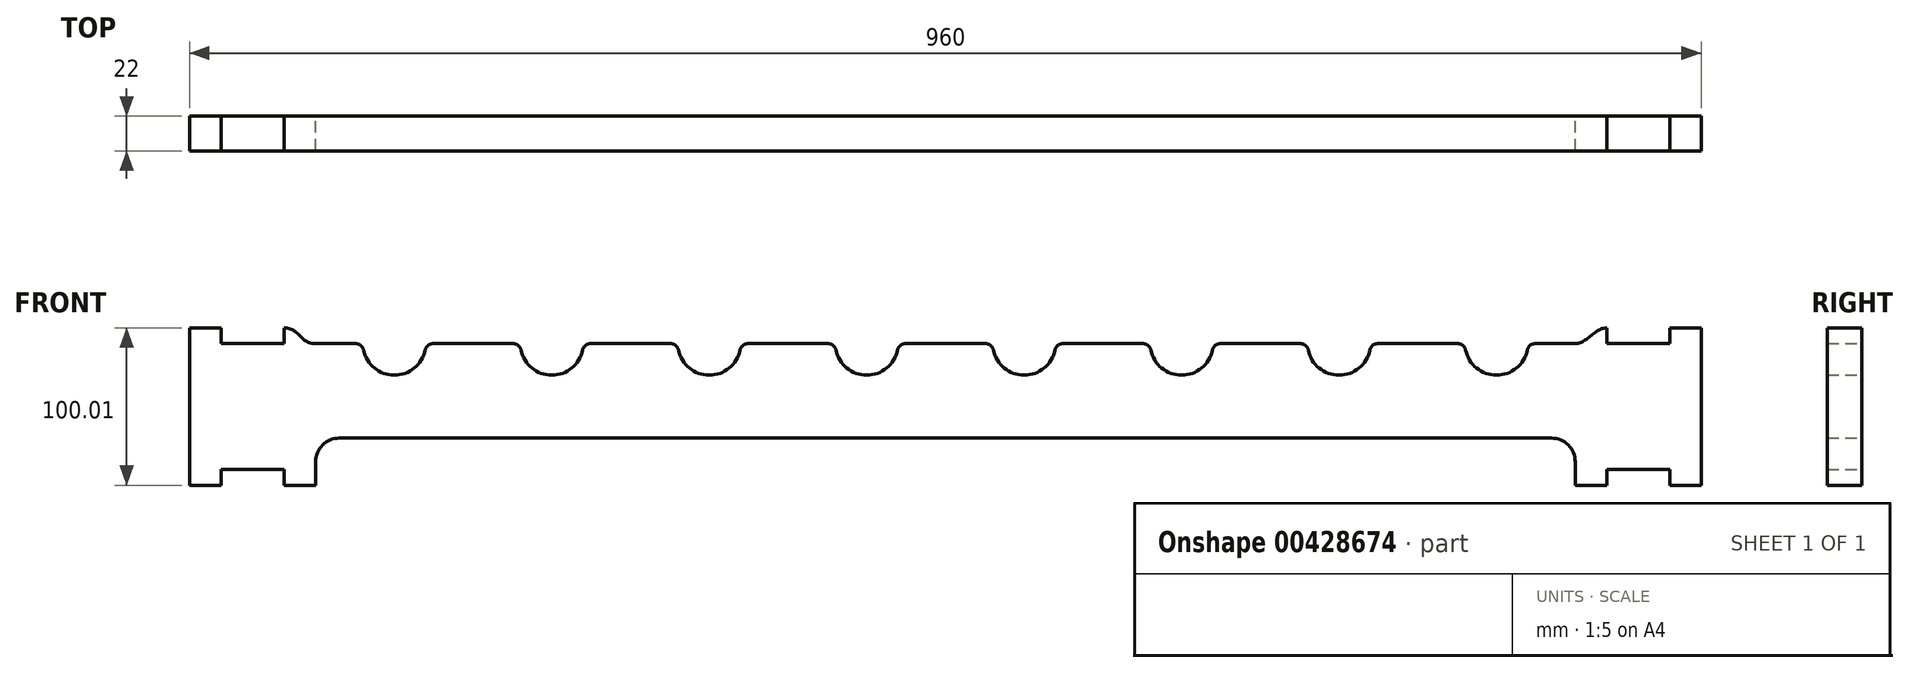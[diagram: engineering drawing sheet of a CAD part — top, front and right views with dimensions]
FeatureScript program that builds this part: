
annotation { "Feature Type Name" : "Feature", "Feature Type Description" : "" }
export const myFeature = defineFeature(function(context is Context, id is Id, definition is map)
    precondition{}
    {
        {
            var Q0;
            Q0=qCreatedBy(makeId("Front.planeOp"),FACE);
            var sketch = newSketch(context, id + "F0", { "sketchPlane" : qUnion([Q0])});
            skLineSegment(sketch, "E0.bottom", {"start": v(476.5, 50) * mm, "end": v(456.5, 50) * mm});
            skLineSegment(sketch, "E0.top", {"start": v(476.5, -50) * mm, "end": v(456.5, -50) * mm});
            skPoint(sketch, "E0.middle", {"position": v(0, 0) * mm});
            skArc(sketch, "E1", {"start": v(-373.1, 36) * mm, "mid": v(-353.5, 20) * mm, "end": v(-333.9, 36) * mm});
            skArc(sketch, "E2", {"start": v(-273.1, 36) * mm, "mid": v(-253.5, 20) * mm, "end": v(-233.9, 36) * mm});
            skArc(sketch, "E3", {"start": v(-173.1, 36) * mm, "mid": v(-153.5, 20) * mm, "end": v(-133.9, 36) * mm});
            skArc(sketch, "E4", {"start": v(-73.1, 36) * mm, "mid": v(-53.5, 20) * mm, "end": v(-33.9, 36) * mm});
            skArc(sketch, "E5", {"start": v(26.9, 36) * mm, "mid": v(46.5, 20) * mm, "end": v(66.1, 36) * mm});
            skArc(sketch, "E6", {"start": v(126.9, 36) * mm, "mid": v(146.5, 20) * mm, "end": v(166.1, 36) * mm});
            skArc(sketch, "E7", {"start": v(226.9, 36) * mm, "mid": v(246.5, 20) * mm, "end": v(266.1, 36) * mm});
            skArc(sketch, "E8", {"start": v(326.9, 36) * mm, "mid": v(346.5, 20) * mm, "end": v(366.1, 36) * mm});
            skLineSegment(sketch, "E9", {"start": v(456.5, 50) * mm, "end": v(476.5, 50) * mm});
            skLineSegment(sketch, "E10", {"start": v(476.5, 50) * mm, "end": v(476.5, -50) * mm});
            skLineSegment(sketch, "E11", {"start": v(416.5, -50) * mm, "end": v(416.5, -40) * mm});
            skLineSegment(sketch, "E12", {"start": v(416.5, -40) * mm, "end": v(456.5, -40) * mm});
            skLineSegment(sketch, "E13", {"start": v(456.5, 40) * mm, "end": v(416.5, 40) * mm});
            skLineSegment(sketch, "E14", {"start": v(416.5, 40) * mm, "end": v(416.5, 50) * mm});
            skLineSegment(sketch, "E15", {"start": v(456.5, 50) * mm, "end": v(456.5, 40) * mm});
            skLineSegment(sketch, "E16", {"start": v(456.5, -40) * mm, "end": v(456.5, -50) * mm});
            skLineSegment(sketch, "E17.trimOffspring", {"start": v(416.5, -50) * mm, "end": v(396.5, -50) * mm});
            skLineSegment(sketch, "E18", {"start": v(-422.71, 50) * mm, "end": v(-423.5, 50) * mm});
            skLineSegment(sketch, "E19", {"start": v(-463.5, 50) * mm, "end": v(-483.5, 50) * mm});
            skLineSegment(sketch, "E20", {"start": v(-483.5, 50) * mm, "end": v(-483.5, -50) * mm});
            skLineSegment(sketch, "E21", {"start": v(-483.5, -50) * mm, "end": v(-463.5, -50) * mm});
            skLineSegment(sketch, "E22", {"start": v(-423.5, -50) * mm, "end": v(-423.5, -40) * mm});
            skLineSegment(sketch, "E23", {"start": v(-423.5, -40) * mm, "end": v(-463.5, -40) * mm});
            skLineSegment(sketch, "E24", {"start": v(-463.5, 40) * mm, "end": v(-423.5, 40) * mm});
            skLineSegment(sketch, "E25", {"start": v(-423.5, 40) * mm, "end": v(-423.5, 50) * mm});
            skLineSegment(sketch, "E26", {"start": v(-463.5, 50) * mm, "end": v(-463.5, 40) * mm});
            skLineSegment(sketch, "E27", {"start": v(-463.5, -40) * mm, "end": v(-463.5, -50) * mm});
            skLineSegment(sketch, "E28.trimOffspring", {"start": v(-463.5, -50) * mm, "end": v(-483.5, -50) * mm});
            skLineSegment(sketch, "E29.trimOffspring", {"start": v(-329, 40) * mm, "end": v(-278, 40) * mm});
            skLineSegment(sketch, "E30.trimOffspring", {"start": v(-229, 40) * mm, "end": v(-178, 40) * mm});
            skLineSegment(sketch, "E31.trimOffspring", {"start": v(-129, 40) * mm, "end": v(-78, 40) * mm});
            skLineSegment(sketch, "E32.trimOffspring", {"start": v(-29, 40) * mm, "end": v(22, 40) * mm});
            skLineSegment(sketch, "E33.trimOffspring", {"start": v(71, 40) * mm, "end": v(122, 40) * mm});
            skLineSegment(sketch, "E34.trimOffspring", {"start": v(171, 40) * mm, "end": v(222, 40) * mm});
            skLineSegment(sketch, "E35.trimOffspring", {"start": v(271, 40) * mm, "end": v(322, 40) * mm});
            skLineSegment(sketch, "E36.trimOffspring", {"start": v(371, 40) * mm, "end": v(396.5, 40) * mm});
            skLineSegment(sketch, "E37", {"start": v(-403.5, 40) * mm, "end": v(-378, 40) * mm});
            skFitSpline(sketch, "E38", {"points": [v(-423.5, 50) * mm, v(-403.5, 40) * mm], "startDerivative": vector(28.84, 0.87) * mm, "endDerivative": vector(30, 0) * mm});
            skFitSpline(sketch, "E39", {"points": [v(396.5, 40) * mm, v(416.5, 50) * mm], "startDerivative": vector(21.98, 0) * mm, "endDerivative": vector(23.53, 0) * mm});
            skPoint(sketch, "E40.trimOffspring.start.orphan", {"position": v(-423.5, 40) * mm});
            skPoint(sketch, "E41.visualSharp", {"position": v(-373.5, 40) * mm});
            skArc(sketch, "E41.filletArc", {"start": v(-373.1, 36) * mm, "mid": v(-374.83, 38.87) * mm, "end": v(-378, 40) * mm});
            skPoint(sketch, "E42.visualSharp", {"position": v(-333.5, 40) * mm});
            skArc(sketch, "E42.filletArc", {"start": v(-329, 40) * mm, "mid": v(-332.17, 38.87) * mm, "end": v(-333.9, 36) * mm});
            skPoint(sketch, "E43.visualSharp", {"position": v(-273.5, 40) * mm});
            skArc(sketch, "E43.filletArc", {"start": v(-273.1, 36) * mm, "mid": v(-274.83, 38.87) * mm, "end": v(-278, 40) * mm});
            skPoint(sketch, "E44.visualSharp", {"position": v(-233.5, 40) * mm});
            skArc(sketch, "E44.filletArc", {"start": v(-229, 40) * mm, "mid": v(-232.17, 38.87) * mm, "end": v(-233.9, 36) * mm});
            skPoint(sketch, "E45.visualSharp", {"position": v(-173.5, 40) * mm});
            skArc(sketch, "E45.filletArc", {"start": v(-173.1, 36) * mm, "mid": v(-174.83, 38.87) * mm, "end": v(-178, 40) * mm});
            skPoint(sketch, "E46.visualSharp", {"position": v(-133.5, 40) * mm});
            skArc(sketch, "E46.filletArc", {"start": v(-129, 40) * mm, "mid": v(-132.17, 38.87) * mm, "end": v(-133.9, 36) * mm});
            skPoint(sketch, "E47.visualSharp", {"position": v(-73.5, 40) * mm});
            skArc(sketch, "E47.filletArc", {"start": v(-73.1, 36) * mm, "mid": v(-74.83, 38.87) * mm, "end": v(-78, 40) * mm});
            skPoint(sketch, "E48.visualSharp", {"position": v(-33.5, 40) * mm});
            skArc(sketch, "E48.filletArc", {"start": v(-29, 40) * mm, "mid": v(-32.17, 38.87) * mm, "end": v(-33.9, 36) * mm});
            skPoint(sketch, "E49.visualSharp", {"position": v(26.5, 40) * mm});
            skArc(sketch, "E49.filletArc", {"start": v(26.9, 36) * mm, "mid": v(25.17, 38.87) * mm, "end": v(22, 40) * mm});
            skPoint(sketch, "E50.visualSharp", {"position": v(66.5, 40) * mm});
            skArc(sketch, "E50.filletArc", {"start": v(71, 40) * mm, "mid": v(67.83, 38.87) * mm, "end": v(66.1, 36) * mm});
            skPoint(sketch, "E51.visualSharp", {"position": v(126.5, 40) * mm});
            skArc(sketch, "E51.filletArc", {"start": v(126.9, 36) * mm, "mid": v(125.17, 38.87) * mm, "end": v(122, 40) * mm});
            skPoint(sketch, "E52.visualSharp", {"position": v(166.5, 40) * mm});
            skArc(sketch, "E52.filletArc", {"start": v(171, 40) * mm, "mid": v(167.83, 38.87) * mm, "end": v(166.1, 36) * mm});
            skPoint(sketch, "E53.visualSharp", {"position": v(226.5, 40) * mm});
            skArc(sketch, "E53.filletArc", {"start": v(226.9, 36) * mm, "mid": v(225.17, 38.87) * mm, "end": v(222, 40) * mm});
            skPoint(sketch, "E54.visualSharp", {"position": v(266.5, 40) * mm});
            skArc(sketch, "E54.filletArc", {"start": v(271, 40) * mm, "mid": v(267.83, 38.87) * mm, "end": v(266.1, 36) * mm});
            skPoint(sketch, "E55.visualSharp", {"position": v(326.5, 40) * mm});
            skArc(sketch, "E55.filletArc", {"start": v(326.9, 36) * mm, "mid": v(325.17, 38.87) * mm, "end": v(322, 40) * mm});
            skPoint(sketch, "E56.visualSharp", {"position": v(366.5, 40) * mm});
            skArc(sketch, "E56.filletArc", {"start": v(371, 40) * mm, "mid": v(367.83, 38.87) * mm, "end": v(366.1, 36) * mm});
            skLineSegment(sketch, "E57", {"start": v(-403.5, -50) * mm, "end": v(-403.5, -35) * mm});
            skLineSegment(sketch, "E58", {"start": v(-388.5, -20) * mm, "end": v(381.5, -20) * mm});
            skLineSegment(sketch, "E59", {"start": v(396.5, -35) * mm, "end": v(396.5, -50) * mm});
            skPoint(sketch, "E60.visualSharp", {"position": v(-403.5, -20) * mm});
            skArc(sketch, "E60.filletArc", {"start": v(-388.5, -20) * mm, "mid": v(-399.1, -24.4) * mm, "end": v(-403.5, -35) * mm});
            skPoint(sketch, "E61.visualSharp", {"position": v(396.5, -20) * mm});
            skArc(sketch, "E61.filletArc", {"start": v(396.5, -35) * mm, "mid": v(392.1, -24.4) * mm, "end": v(381.5, -20) * mm});
            skLineSegment(sketch, "E62.trimOffspring", {"start": v(-403.5, -50) * mm, "end": v(-423.5, -50) * mm});
            skSolve(sketch);
        }
        {
            var Q0;
            Q0 = qSketchRegion(id + "F0", true);
            extrude(context, id + "F1", {"entities" : qUnion([Q0]), "depth" : 22 * mm});
        }
    });
